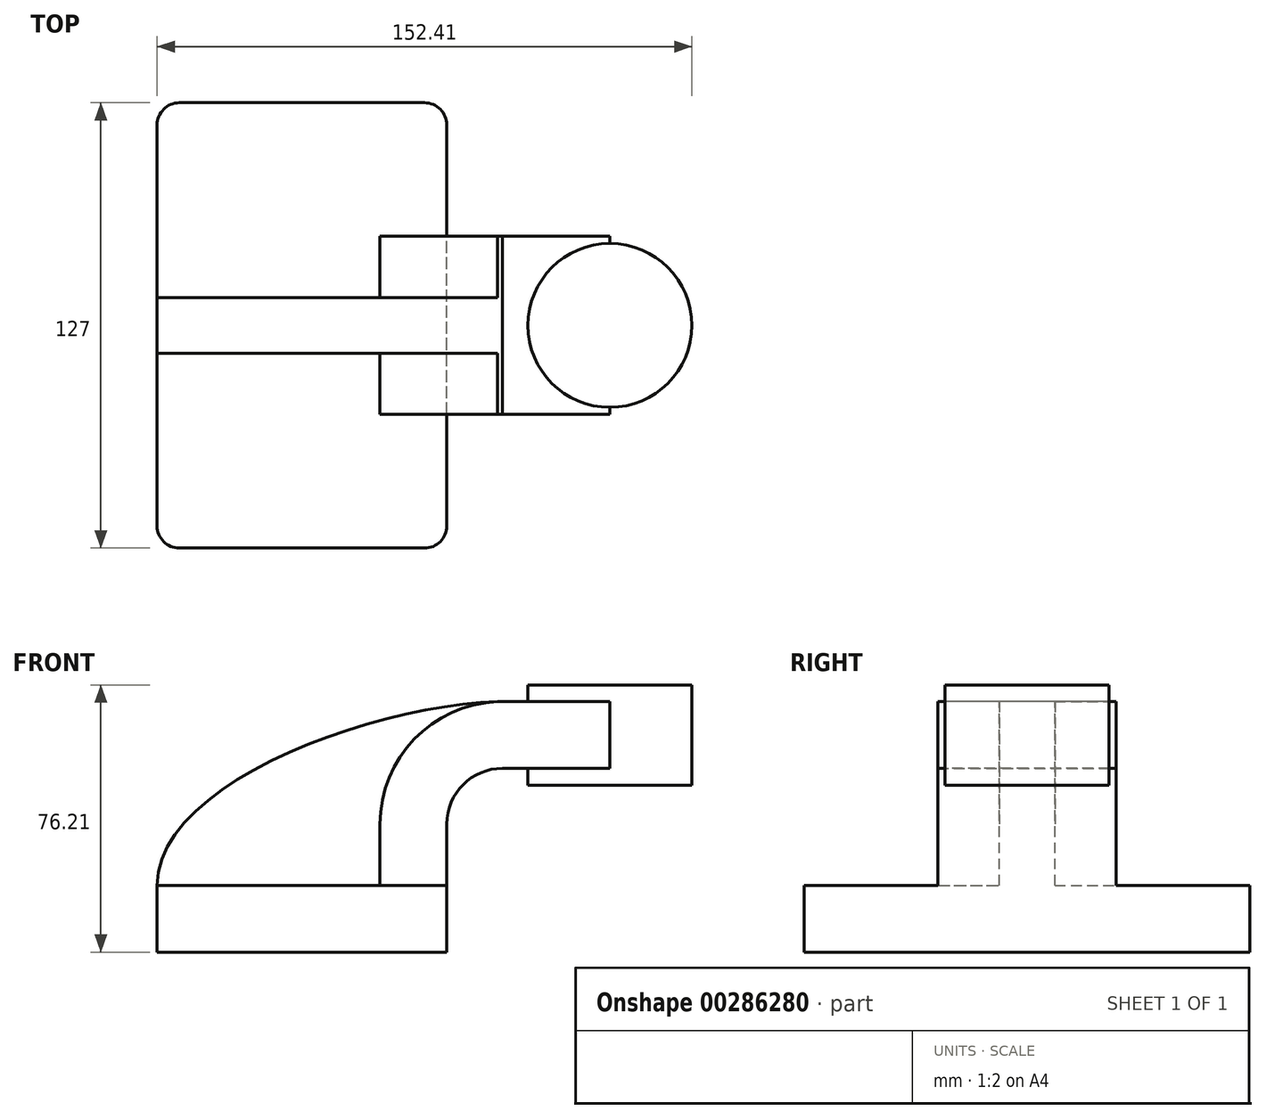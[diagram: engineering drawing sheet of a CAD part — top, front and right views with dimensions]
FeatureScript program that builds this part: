
annotation { "Feature Type Name" : "Feature", "Feature Type Description" : "" }
export const myFeature = defineFeature(function(context is Context, id is Id, definition is map)
    precondition{}
    {
        {
            var Q0;
            Q0=qCreatedBy(makeId("Front.planeOp"),FACE);
            var sketch = newSketch(context, id + "F0", { "sketchPlane" : qUnion([Q0])});
            skSolve(sketch);
        }
        {
            var Q0;
            Q0=qCreatedBy(makeId("Front.planeOp"),FACE);
            var sketch = newSketch(context, id + "F1", { "sketchPlane" : qUnion([Q0])});
            skLineSegment(sketch, "E0.bottom", {"start": v(41.27, 9.53) * mm, "end": v(-41.28, 9.53) * mm});
            skLineSegment(sketch, "E0.top", {"start": v(41.28, -9.52) * mm, "end": v(-41.27, -9.52) * mm});
            skLineSegment(sketch, "E0.left", {"start": v(41.28, 9.53) * mm, "end": v(41.28, -9.52) * mm});
            skLineSegment(sketch, "E0.right", {"start": v(-41.28, 9.53) * mm, "end": v(-41.27, -9.52) * mm});
            skPoint(sketch, "E0.middle", {"position": v(0, 0) * mm});
            skLineSegment(sketch, "E1.bottom", {"start": v(111.13, 38.1) * mm, "end": v(60.32, 38.1) * mm});
            skLineSegment(sketch, "E1.top", {"start": v(111.13, 66.68) * mm, "end": v(60.33, 66.68) * mm});
            skLineSegment(sketch, "E1.left", {"start": v(111.13, 38.1) * mm, "end": v(111.13, 66.68) * mm});
            skLineSegment(sketch, "E1.right", {"start": v(60.33, 38.1) * mm, "end": v(60.33, 66.68) * mm});
            skPoint(sketch, "E1.middle", {"position": v(85.73, 52.39) * mm});
            skLineSegment(sketch, "E2", {"start": v(41.27, 9.53) * mm, "end": v(41.27, 27) * mm});
            skArc(sketch, "E3", {"start": v(41.27, 27) * mm, "mid": v(45.92, 38.23) * mm, "end": v(57.15, 42.88) * mm});
            skLineSegment(sketch, "E4", {"start": v(57.15, 42.88) * mm, "end": v(87.75, 42.88) * mm});
            skLineSegment(sketch, "E5.0", {"start": v(57.15, 61.93) * mm, "end": v(87.75, 61.93) * mm});
            skArc(sketch, "E5.1", {"start": v(22.23, 27) * mm, "mid": v(32.45, 51.7) * mm, "end": v(57.15, 61.93) * mm});
            skLineSegment(sketch, "E5.2", {"start": v(22.23, 9.53) * mm, "end": v(22.23, 27) * mm});
            skLineSegment(sketch, "E6", {"start": v(87.75, 38.1) * mm, "end": v(87.75, 66.68) * mm});
            skPoint(sketch, "E6.startSnap0", {"position": v(85.73, 38.1) * mm});
            skFitSpline(sketch, "E7", {"points": [v(-41.28, 9.53) * mm, v(57.15, 61.93) * mm], "startDerivative": vector(-0.2, 88.2) * mm, "endDerivative": vector(106.98, 1.31) * mm});
            skSolve(sketch);
        }
        {
            var Q0;
            Q0=makeQuery(id+"F1.imprint","IMPRINT",FACE,{"disambiguationData":[TD([[makeQuery(id+"F1.imprint","IMPRINT",EDGE,{"derivedFrom":sQuery(id+"F1.wireOp",EDGE,"E0.top")}),-1.0]])]});
            var Q1;
            Q1 = qSketchRegion(id + "F0", true);
            extrude(context, id + "F2", {"entities" : qUnion([Q0, Q1]), "endBound" : BoundingType.SYMMETRIC, "depth" : 127 * mm});
        }
        {
            var Q0;
            {var subQ1=sQuery(id+"F1.wireOp",EDGE,"E2");Q0=makeQuery(id+"F1.imprint","IMPRINT",FACE,{"disambiguationData":[TD([[makeQuery(id+"F1.imprint","IMPRINT",EDGE,{"derivedFrom":subQ1}),1.0]])]});}
            var Q1;
            {var subQ0=sQuery(id+"F1.wireOp",EDGE,"E4");var subQ1=sQuery(id+"F1.wireOp",EDGE,"E1.right");var subQ2=makeQuery(id+"F1.imprint","INTERSECT",VERTEX,{"derivedFrom":[subQ1,subQ0]});Q1=makeQuery(id+"F1.imprint","IMPRINT",FACE,{"disambiguationData":[TD([[makeQuery(id+"F1.imprint","IMPRINT",EDGE,{"disambiguationData":[TD([[subQ2,-1.0]])],"derivedFrom":subQ1}),-1.0]])]});}
            extrude(context, id + "F3", {"entities" : qUnion([Q0, Q1]), "operationType" : NewBodyOperationType.ADD, "endBound" : BoundingType.SYMMETRIC, "depth" : 50.8 * mm});
        }
        {
            var Q0;
            {var subQ3=sQuery(id+"F1.wireOp",EDGE,"E5.2");Q0=makeQuery(id+"F1.imprint","IMPRINT",FACE,{"disambiguationData":[TD([[makeQuery(id+"F1.imprint","IMPRINT",EDGE,{"derivedFrom":subQ3}),1.0]])]});}
            extrude(context, id + "F4", {"entities" : qUnion([Q0]), "operationType" : NewBodyOperationType.ADD, "endBound" : BoundingType.SYMMETRIC, "depth" : 15.88 * mm});
        }
        {
            var Q0;
            {var subQ0=sQuery(id+"F1.wireOp",EDGE,"E1.left");Q0=makeQuery(id+"F1.imprint","IMPRINT",FACE,{"disambiguationData":[TD([[makeQuery(id+"F1.imprint","IMPRINT",EDGE,{"derivedFrom":subQ0}),1.0]])]});}
            var Q1;
            Q1=sQuery(id+"F1.wireOp",EDGE,"E6");
            revolve(context, id + "F5", {"operationType" : NewBodyOperationType.ADD, "entities" : qUnion([Q0]), "axis" : qUnion([Q1]), "revolveType" : RevolveType.FULL});
        }
        {
            var Q0;
            Q0=makeQuery(id+"F2.opExtrude","CAP_EDGE",EDGE,{"disambiguationData":[OSD([sQuery(id+"F1.wireOp",EDGE,"E0.left")])],"isStart":false});
            var Q1;
            Q1=makeQuery(id+"F2.opExtrude","CAP_EDGE",EDGE,{"disambiguationData":[OSD([sQuery(id+"F1.wireOp",EDGE,"E0.right")])],"isStart":false});
            var Q2;
            Q2=makeQuery(id+"F2.opExtrude","CAP_EDGE",EDGE,{"disambiguationData":[OSD([sQuery(id+"F1.wireOp",EDGE,"E0.right")])],"isStart":true});
            var Q3;
            Q3=makeQuery(id+"F2.opExtrude","CAP_EDGE",EDGE,{"disambiguationData":[OSD([sQuery(id+"F1.wireOp",EDGE,"E0.left")])],"isStart":true});
            fillet(context, id + "F6", {"entities" : qUnion([Q0, Q1, Q2, Q3]), "radius" : 6.35 * mm, "tangentPropagation" : true, "allowEdgeOverflow" : false});
        }
    });
